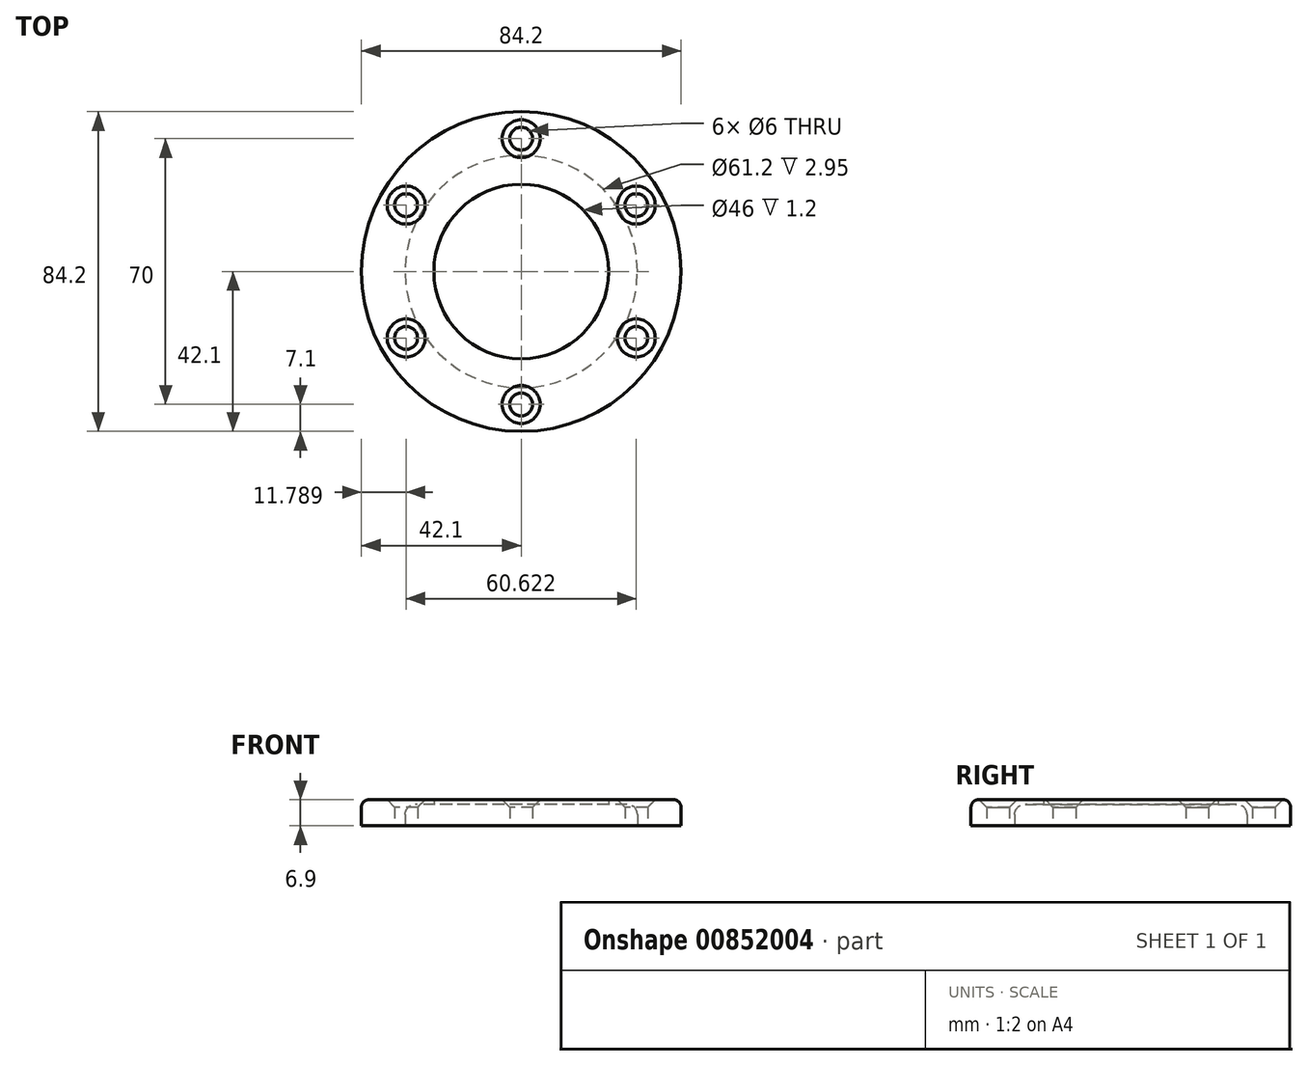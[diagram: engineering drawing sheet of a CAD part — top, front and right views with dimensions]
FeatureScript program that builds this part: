
annotation { "Feature Type Name" : "Feature", "Feature Type Description" : "" }
export const myFeature = defineFeature(function(context is Context, id is Id, definition is map)
    precondition{}
    {
        {
            var Q0;
            Q0=qCreatedBy(makeId("Top.planeOp"),FACE);
            var sketch = newSketch(context, id + "F0", { "sketchPlane" : qUnion([Q0])});
            skCircle(sketch, "E0", {"center": v(0, 0) * mm, "radius": 30.6 * mm});
            skSolve(sketch);
        }
        {
            var Q0;
            Q0 = qSketchRegion(id + "F0", true);
            extrude(context, id + "F1", {"entities" : qUnion([Q0]), "depth" : 5.7 * mm, "offsetDistance" : 25 * mm});
        }
        {
            var Q0;
            Q0=makeQuery(id+"F1.opExtrude","CAP_FACE",FACE,{"disambiguationData":[OSD([sQuery(id+"F0.wireOp",EDGE,"E0")])],"isStart":false});
            var sketch = newSketch(context, id + "F2", { "sketchPlane" : qUnion([Q0])});
            skCircle(sketch, "E1", {"center": v(0, 0) * mm, "radius": 23 * mm});
            skSolve(sketch);
        }
        {
            var Q0;
            Q0 = qSketchRegion(id + "F2", true);
            extrude(context, id + "F3", {"entities" : qUnion([Q0]), "operationType" : NewBodyOperationType.ADD, "depth" : 1.2 * mm, "offsetDistance" : 25 * mm});
        }
        {
            var Q0;
            Q0=makeQuery(id+"F1.opExtrude","CAP_EDGE",EDGE,{"disambiguationData":[OSD([sQuery(id+"F0.wireOp",EDGE,"E0")])],"isStart":false});
            fillet(context, id + "F4", {"entities" : qUnion([Q0]), "radius" : 2.75 * mm, "tangentPropagation" : true, "allowEdgeOverflow" : false});
        }
        {
            var Q0;
            Q0=qCreatedBy(makeId("Top.planeOp"),FACE);
            var sketch = newSketch(context, id + "F5", { "sketchPlane" : qUnion([Q0])});
            skCircle(sketch, "E2", {"center": v(0, 0) * mm, "radius": 42.1 * mm});
            skCircle(sketch, "E3", {"center": v(0, 0) * mm, "radius": 35 * mm, "construction": true});
            skCircle(sketch, "E4", {"center": v(0, -35) * mm, "radius": 3 * mm});
            skCircle(sketch, "E5.1.0", {"center": v(30.31, -17.5) * mm, "radius": 3 * mm});
            skCircle(sketch, "E5.2.0", {"center": v(30.31, 17.5) * mm, "radius": 3 * mm});
            skCircle(sketch, "E5.3.0", {"center": v(0, 35) * mm, "radius": 3 * mm});
            skCircle(sketch, "E5.4.0", {"center": v(-30.31, 17.5) * mm, "radius": 3 * mm});
            skCircle(sketch, "E5.5.0", {"center": v(-30.31, -17.5) * mm, "radius": 3 * mm});
            skSolve(sketch);
        }
        {
            var Q0;
            Q0=makeQuery(id+"F5.imprint","IMPRINT",FACE,{"disambiguationData":[TD([[makeQuery(id+"F5.imprint","IMPRINT",EDGE,{"derivedFrom":sQuery(id+"F5.wireOp",EDGE,"E2")}),1.0]])]});
            var Q1;
            Q1=makeQuery(id+"F3.opExtrude","CAP_FACE",FACE,{"disambiguationData":[OSD([sQuery(id+"F2.wireOp",EDGE,"E1")])],"isStart":false});
            extrude(context, id + "F6", {"entities" : qUnion([Q0]), "endBound" : BoundingType.UP_TO_SURFACE, "depth" : 25 * mm, "endBoundEntityFace" : qUnion([Q1]), "offsetDistance" : 25 * mm});
        }
        {
            var Q0;
            Q0=makeQuery(id+"F1.opExtrude","SWEPT_BODY",BODY,{"disambiguationData":[OSD([sQuery(id+"F0.wireOp",EDGE,"E0")])]});
            var Q1;
            Q1=makeQuery(id+"F6.opExtrude","SWEPT_BODY",BODY,{"disambiguationData":[OSD([sQuery(id+"F5.wireOp",EDGE,"E2"),sQuery(id+"F5.wireOp",EDGE,"E4"),sQuery(id+"F5.wireOp",EDGE,"E5.1.0"),sQuery(id+"F5.wireOp",EDGE,"E5.2.0"),sQuery(id+"F5.wireOp",EDGE,"E5.3.0"),sQuery(id+"F5.wireOp",EDGE,"E5.4.0"),sQuery(id+"F5.wireOp",EDGE,"E5.5.0")])]});
            booleanBodies(context, id + "F7", {"operationType" : BooleanOperationType.SUBTRACTION, "tools" : qUnion([Q0]), "targets" : qUnion([Q1]), "keepTools" : true});
        }
        {
            var Q0;
            Q0=makeQuery(id+"F6.opExtrude","CAP_FACE",FACE,{"disambiguationData":[OSD([sQuery(id+"F5.wireOp",EDGE,"E2"),sQuery(id+"F5.wireOp",EDGE,"E4"),sQuery(id+"F5.wireOp",EDGE,"E5.1.0"),sQuery(id+"F5.wireOp",EDGE,"E5.2.0"),sQuery(id+"F5.wireOp",EDGE,"E5.3.0"),sQuery(id+"F5.wireOp",EDGE,"E5.4.0"),sQuery(id+"F5.wireOp",EDGE,"E5.5.0")])],"isStart":false});
            var sketch = newSketch(context, id + "F8", { "sketchPlane" : qUnion([Q0])});
            skCircle(sketch, "E6", {"center": v(-30.31, -17.5) * mm, "radius": 5 * mm});
            skCircle(sketch, "E7.1.0", {"center": v(0, -35) * mm, "radius": 5 * mm});
            skCircle(sketch, "E7.2.0", {"center": v(30.31, -17.5) * mm, "radius": 5 * mm});
            skCircle(sketch, "E7.3.0", {"center": v(30.31, 17.5) * mm, "radius": 5 * mm});
            skCircle(sketch, "E7.4.0", {"center": v(0, 35) * mm, "radius": 5 * mm});
            skCircle(sketch, "E7.5.0", {"center": v(-30.31, 17.5) * mm, "radius": 5 * mm});
            skPoint(sketch, "E7.center", {"position": v(0, 0) * mm});
            skSolve(sketch);
        }
        {
            var Q0;
            Q0 = qSketchRegion(id + "F8", true);
            extrude(context, id + "F9", {"entities" : qUnion([Q0]), "operationType" : NewBodyOperationType.REMOVE, "oppositeDirection" : true, "depth" : 25 * mm, "offsetDistance" : 25 * mm, "hasDraft" : true, "draftAngle" : 45 * degree, "draftPullDirection" : true});
        }
        {
            var Q0;
            Q0=makeQuery(id+"F6.opExtrude","CAP_EDGE",EDGE,{"disambiguationData":[OSD([sQuery(id+"F5.wireOp",EDGE,"E2")])],"isStart":false});
            fillet(context, id + "F10", {"entities" : qUnion([Q0]), "radius" : 2 * mm, "tangentPropagation" : true, "allowEdgeOverflow" : false});
        }
    });
